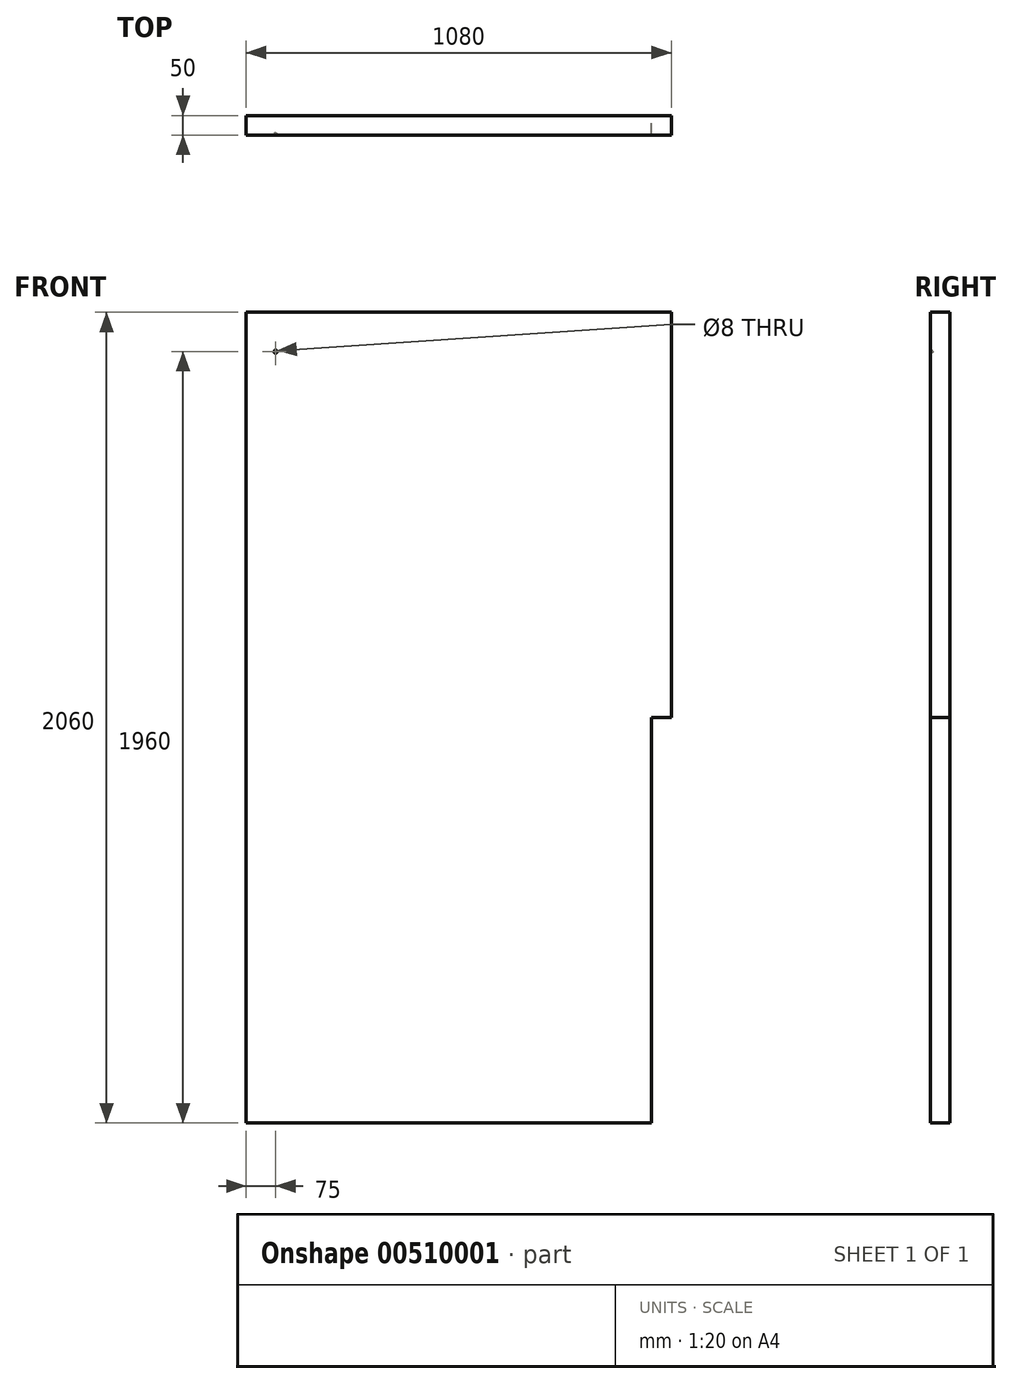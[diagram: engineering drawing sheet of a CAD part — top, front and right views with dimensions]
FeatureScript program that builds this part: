
annotation { "Feature Type Name" : "Feature", "Feature Type Description" : "" }
export const myFeature = defineFeature(function(context is Context, id is Id, definition is map)
    precondition{}
    {
        {
            var Q0;
            Q0=qCreatedBy(makeId("Front.planeOp"),FACE);
            var sketch = newSketch(context, id + "F0", { "sketchPlane" : qUnion([Q0])});
            skLineSegment(sketch, "E0.bottom", {"start": v(-1004.84, 2005.49) * mm, "end": v(75.16, 2005.49) * mm});
            skLineSegment(sketch, "E0.top", {"start": v(-1004.84, -54.51) * mm, "end": v(25.16, -54.51) * mm});
            skLineSegment(sketch, "E0.left", {"start": v(-1004.84, 2005.49) * mm, "end": v(-1004.84, -54.51) * mm});
            skLineSegment(sketch, "E0.right", {"start": v(75.16, 2005.49) * mm, "end": v(75.16, 975.49) * mm});
            skLineSegment(sketch, "E1.top", {"start": v(75.16, 975.49) * mm, "end": v(25.16, 975.49) * mm});
            skLineSegment(sketch, "E1.right", {"start": v(25.16, -54.51) * mm, "end": v(25.16, 975.49) * mm});
            skSolve(sketch);
        }
        {
            var Q0;
            Q0=makeQuery(id+"F0.imprint","IMPRINT",FACE,{"disambiguationData":[TD([[makeQuery(id+"F0.imprint","IMPRINT",EDGE,{"derivedFrom":sQuery(id+"F0.wireOp",EDGE,"E0.bottom")}),-1.0]])]});
            extrude(context, id + "F1", {"entities" : qUnion([Q0]), "depth" : 50 * mm});
        }
        {
            var Q0;
            Q0=makeQuery(id+"F1.opExtrude","CAP_FACE",FACE,{"disambiguationData":[OSD([sQuery(id+"F0.wireOp",EDGE,"E0.bottom"),sQuery(id+"F0.wireOp",EDGE,"E0.top"),sQuery(id+"F0.wireOp",EDGE,"E0.left"),sQuery(id+"F0.wireOp",EDGE,"E0.right"),sQuery(id+"F0.wireOp",EDGE,"E1.top"),sQuery(id+"F0.wireOp",EDGE,"E1.right")])],"isStart":false});
            var sketch = newSketch(context, id + "F2", { "sketchPlane" : qUnion([Q0])});
            skCircle(sketch, "E2", {"center": v(-929.84, 1905.49) * mm, "radius": 4 * mm});
            skSolve(sketch);
        }
        {
            var Q0;
            Q0=sQuery(id+"F2.wireOp",VERTEX,"E2.center");
            var Q1;
            Q1=makeQuery(id+"F1.opExtrude","SWEPT_BODY",BODY,{"disambiguationData":[OSD([sQuery(id+"F0.wireOp",EDGE,"E0.bottom"),sQuery(id+"F0.wireOp",EDGE,"E0.top"),sQuery(id+"F0.wireOp",EDGE,"E0.left"),sQuery(id+"F0.wireOp",EDGE,"E0.right"),sQuery(id+"F0.wireOp",EDGE,"E1.top"),sQuery(id+"F0.wireOp",EDGE,"E1.right")])]});
            hole(context, id + "F3", {"style" : HoleStyle.SIMPLE, "endStyle" : HoleEndStyle.BLIND, "holeDiameter" : 8 * mm, "holeDepth" : 4 * mm, "isTappedThrough" : true, "tappedDepth" : 12 * mm, "tapClearance" : 3, "locations" : qUnion([Q0]), "scope" : qUnion([Q1])});
        }
    });
